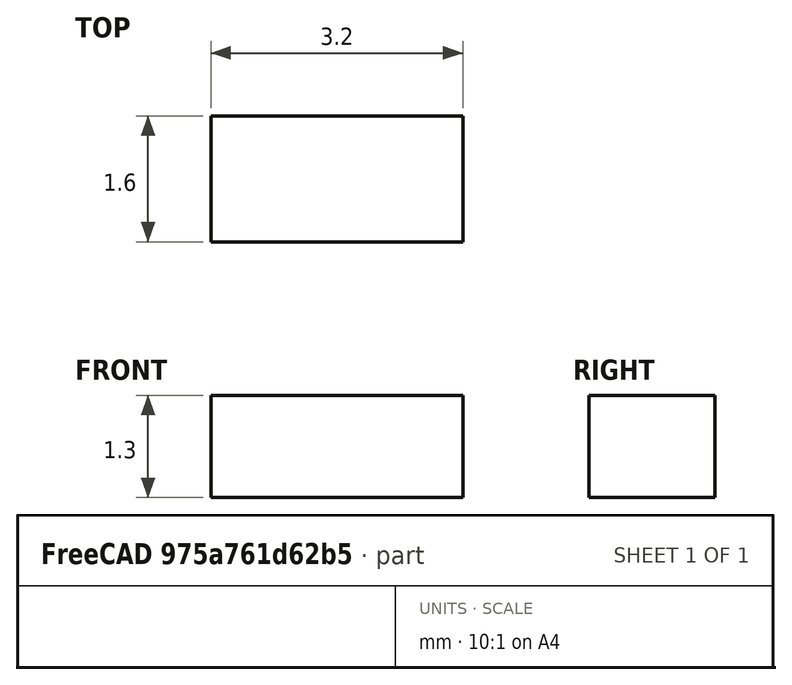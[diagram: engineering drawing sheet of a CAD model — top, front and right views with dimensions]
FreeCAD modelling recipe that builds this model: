
FCSTD DOCUMENT  (FreeCAD 0.16R6707 (Git))
Label: chip_ant_32x16
License: All rights reserved
LicenseURL: http://en.wikipedia.org/wiki/All_rights_reserved
objects: Sketcher::SketchObject×1, PartDesign::Pad×1
note: 3 computed .brp shape members not serialized (recipe doc carries the construction recipe); baked Part::Feature solids carry a one-line shape summary decoded from their .brp

FEATURE [Sketcher::SketchObject] Sketch
  sketch-geometry (5):
    g0: LineSegment StartX=-1.6 StartY=0.8 StartZ=0 EndX=1.6 EndY=0.8 EndZ=0
    g1: LineSegment StartX=1.6 StartY=0.8 StartZ=0 EndX=1.6 EndY=-0.8 EndZ=0
    g2: LineSegment StartX=1.6 StartY=-0.8 StartZ=0 EndX=-1.6 EndY=-0.8 EndZ=0
    g3: LineSegment StartX=-1.6 StartY=-0.8 StartZ=0 EndX=-1.6 EndY=0.8 EndZ=0
    g4: LineSegment [constr] StartX=0 StartY=0 StartZ=0 EndX=0 EndY=2.06425 EndZ=0
  constraints (14):
    c: Coincident(g0,g1)
    c: Coincident(g1,g2)
    c: Coincident(g2,g3)
    c: Coincident(g3,g0)
    c: Horizontal(g0)
    c: Horizontal(g2)
    c: Vertical(g1)
    c: Vertical(g3)
    c: DistanceX(g0,g0) = 3.2
    c: DistanceY(g3,g3) = 1.6
    c: Coincident(g4,g-1)
    c: Vertical(g4)
    c: Symmetric(g0,g0,g4)
    c: Symmetric(g1,g0,g-1)
FEATURE [PartDesign::Pad] Pad
  Length = 1.3
  Length2 = 100
  Sketch = -> Sketch
  Type = 0
